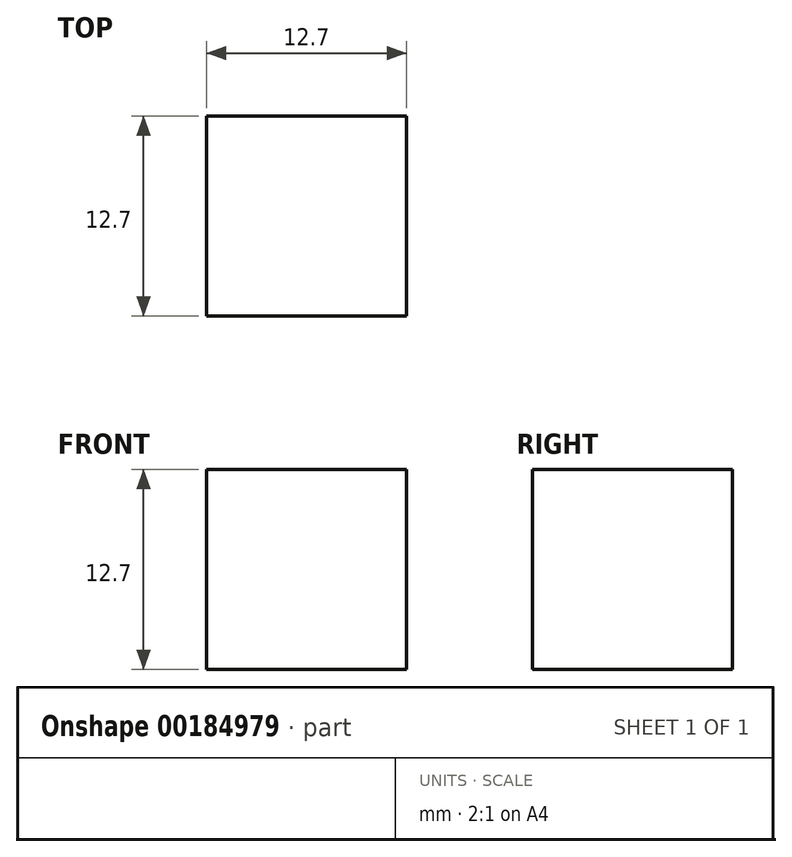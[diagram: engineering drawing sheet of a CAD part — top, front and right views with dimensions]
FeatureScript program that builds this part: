
annotation { "Feature Type Name" : "Feature", "Feature Type Description" : "" }
export const myFeature = defineFeature(function(context is Context, id is Id, definition is map)
    precondition{}
    {
        {
            var Q0;
            Q0=qCreatedBy(makeId("Top.planeOp"),FACE);
            var sketch = newSketch(context, id + "F0", { "sketchPlane" : qUnion([Q0])});
            skLineSegment(sketch, "E0.bottom", {"start": v(-141.84, -25.64) * mm, "end": v(-129.14, -25.64) * mm});
            skLineSegment(sketch, "E0.top", {"start": v(-141.84, -12.94) * mm, "end": v(-129.14, -12.94) * mm});
            skLineSegment(sketch, "E0.left", {"start": v(-141.84, -25.64) * mm, "end": v(-141.84, -12.94) * mm});
            skLineSegment(sketch, "E0.right", {"start": v(-129.14, -25.64) * mm, "end": v(-129.14, -12.94) * mm});
            skSolve(sketch);
        }
        {
            var Q0;
            Q0 = qSketchRegion(id + "F0", true);
            extrude(context, id + "F1", {"entities" : qUnion([Q0]), "depth" : 12.7 * mm});
        }
    });
